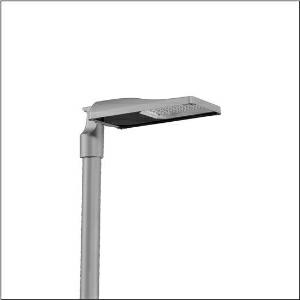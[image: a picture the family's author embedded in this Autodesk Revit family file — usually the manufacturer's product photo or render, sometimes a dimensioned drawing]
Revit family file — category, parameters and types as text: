
# Revit family: streetlight_sl_31_mini___st1_0a_5xh2d3aa08ha_083f
name_source: partatom
category: Lighting Fixtures
units: mm (PartAtom-declared; Revit-internal decimal feet)

## family parameters
Cut with Voids When Loaded = No
Host = Face
Light Source = No
Part Type = Normal
Room Calculation Point = No
Round Connector Dimension = Use Diameter
Shared = No

## types (1)
- --- (1 x LED, 9240 lm, 68.3 W, 3000K)
    Apparent Load = 68 VA
    CIE Flux Codes = 37 72 97 100 100
    Color Rendering = 70
    Color Temperature = 3000K
    Default Elevation = 1800 mm
    Description = Streetlight SL 31 mini Easy mast luminaire for post-top, side-entry; light control with lens of PMMA; light distribution: ST1.0a, direct asymmetric distribution, for standard-compliant lighting for roads and squares; LED: luminous flux: 9.240lm, light colour: 730, colour temperature: 3000K; luminous efficacy: 135,3lm/W; control: overheat protection, intelligent temperature release in ECG and LED module, constant luminous flux control, time-dependent luminous flux control, flexible luminous flux parameterisation, pre-setting: linear dimming characteristic; luminaire housing, of diecast aluminium, Siteco® metallic grey (DB 702S), corrosivity category C5 high according to DIN EN ISO 12944; cover of toughened safety glass, transparent, mast flange of diecast aluminium, Siteco® metallic grey (DB 702S), spigot size: 76/60mm, mast flange included unmounted; with cable H07RN-F 2x 1.5mm², cable length: 8,5m, connection cable pre-assembled; mains connection: 220..240V, AC, 50/60Hz; power consumption (at start of service life): 68,3W / (at end of service life): 74,8W / (with reduced operation 50%): 29,7W; protection rating (complete): IP66; insulation class (complete): insulation class II (safety insulation); impact resistance: IK10; certification: CE, ENEC, ENEC+, VDE, UKCA; permissible operating ambient temperature for outdoor applications: -40..+50°C; packaging unit: 1 piece

Light Distribution: ST1.0a
    Height = 76 mm
    Lamp = 1 x LED
    Lamp Light Flux = 9240 lm
    Lamp Power = 68.3 W
    Lamp count = 1
    Length = 547 mm
    Luminous efficacy = 135 lm/W
    Manufacturer = Siteco
    ModVariant = No
    Model = 5XH2D3AA08HA
    Number of Poles = 1
    OnlyDefault = Yes
    Power Factor = 1
    Product Name = Streetlight SL 31 mini | ST1.0a
    Product group = mast luminaire | pylon top
    ProductGroupID = 6100
    Protection Class = Protection class II
    Protection Degree = IP 66
    RLX_Detail_Level = 1
    RLX_Emergency_Light_Flux = 0 lm
    RLX_Emergency_Type = 0
    RLX_Emergency_Type_DB = No
    RlxData = <blob elided: 39369 chars, md5=efe98a1d>
    Socket = socket
    Standby Power = 0 W
    System Light Flux = 9240 lm
    System Power = 68 W
    Type Comments = factory setting: luminous flux: 100 % | dim-lin: 254 | 693 mA
    Type Image = l_1300326.jpg
    URL = http://relux.com
    VarID = @adj_055178
    Voltage = 0 V
    Weight = 0.00 kg
    Width = 265 mm

## geometry (parser evidence)
native form markers: Blend x4, Sweep x9
no freeform markers — native parametric forms only
